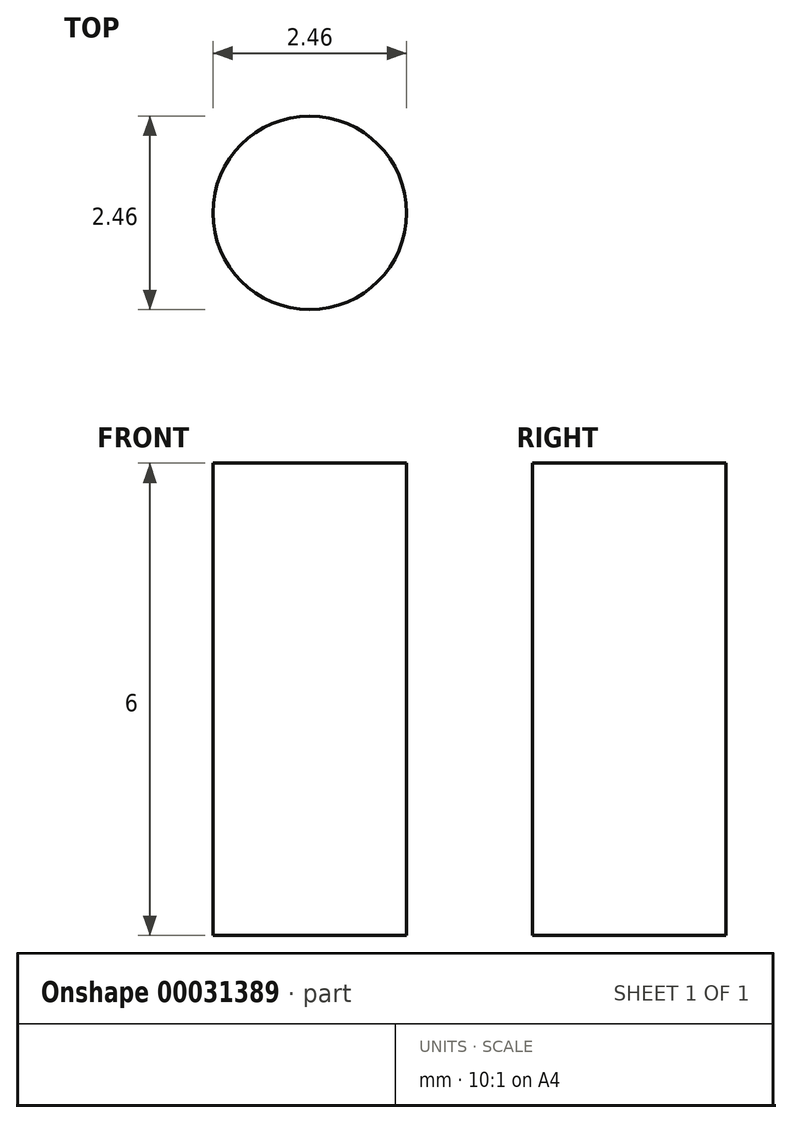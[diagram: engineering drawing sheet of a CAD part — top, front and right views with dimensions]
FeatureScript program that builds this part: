
annotation { "Feature Type Name" : "Feature", "Feature Type Description" : "" }
export const myFeature = defineFeature(function(context is Context, id is Id, definition is map)
    precondition{}
    {
        {
            var Q0;
            Q0=qCreatedBy(makeId("Top.planeOp"),FACE);
            var sketch = newSketch(context, id + "F0", { "sketchPlane" : qUnion([Q0])});
            skCircle(sketch, "E0", {"center": v(-104.5, -104.5) * mm, "radius": 1.23 * mm});
            skCircle(sketch, "E1", {"center": v(104.5, -104.5) * mm, "radius": 1.23 * mm});
            skCircle(sketch, "E2", {"center": v(104.5, 104.5) * mm, "radius": 1.23 * mm});
            skCircle(sketch, "E3", {"center": v(21, 0) * mm, "radius": 1.23 * mm});
            skCircle(sketch, "E4", {"center": v(-20, 0) * mm, "radius": 1.23 * mm});
            skCircle(sketch, "E5", {"center": v(-104.5, 104.5) * mm, "radius": 1.23 * mm});
            skLineSegment(sketch, "E6", {"start": v(75, -68) * mm, "end": v(35, -28) * mm});
            skLineSegment(sketch, "E7", {"start": v(75, 68) * mm, "end": v(75, -68) * mm});
            skLineSegment(sketch, "E8", {"start": v(35, 28) * mm, "end": v(75, 68) * mm});
            skLineSegment(sketch, "E9", {"start": v(35, -28) * mm, "end": v(35, 28) * mm});
            skLineSegment(sketch, "E10", {"start": v(-75, 68) * mm, "end": v(-35, 28) * mm});
            skLineSegment(sketch, "E11", {"start": v(-75, -68) * mm, "end": v(-75, 68) * mm});
            skLineSegment(sketch, "E12", {"start": v(-35, -28) * mm, "end": v(-75, -68) * mm});
            skLineSegment(sketch, "E13", {"start": v(-35, 28) * mm, "end": v(-35, -28) * mm});
            skLineSegment(sketch, "E14", {"start": v(5, -80) * mm, "end": v(-5, -80) * mm});
            skLineSegment(sketch, "E15", {"start": v(25, -60) * mm, "end": v(5, -80) * mm});
            skLineSegment(sketch, "E16", {"start": v(25, -40) * mm, "end": v(25, -60) * mm});
            skLineSegment(sketch, "E17", {"start": v(5, -20) * mm, "end": v(25, -40) * mm});
            skLineSegment(sketch, "E18", {"start": v(-5, -20) * mm, "end": v(5, -20) * mm});
            skLineSegment(sketch, "E19", {"start": v(-25, -40) * mm, "end": v(-5, -20) * mm});
            skLineSegment(sketch, "E20", {"start": v(-25, -60) * mm, "end": v(-25, -40) * mm});
            skLineSegment(sketch, "E21", {"start": v(-5, -80) * mm, "end": v(-25, -60) * mm});
            skLineSegment(sketch, "E22", {"start": v(-25, 40) * mm, "end": v(-25, 50) * mm});
            skLineSegment(sketch, "E23", {"start": v(-5, 20) * mm, "end": v(-25, 40) * mm});
            skLineSegment(sketch, "E24", {"start": v(5, 20) * mm, "end": v(-5, 20) * mm});
            skLineSegment(sketch, "E25", {"start": v(25, 40) * mm, "end": v(5, 20) * mm});
            skLineSegment(sketch, "E26", {"start": v(25, 50) * mm, "end": v(25, 40) * mm});
            skLineSegment(sketch, "E27", {"start": v(5, 70) * mm, "end": v(25, 50) * mm});
            skLineSegment(sketch, "E28", {"start": v(-5, 70) * mm, "end": v(5, 70) * mm});
            skLineSegment(sketch, "E29", {"start": v(-25, 50) * mm, "end": v(-5, 70) * mm});
            skArc(sketch, "E30", {"start": v(46, -90) * mm, "mid": v(48.83, -88.83) * mm, "end": v(50, -86) * mm});
            skLineSegment(sketch, "E31", {"start": v(50, -84) * mm, "end": v(50, -86) * mm});
            skArc(sketch, "E32", {"start": v(50, -84) * mm, "mid": v(48.83, -81.17) * mm, "end": v(46, -80) * mm});
            skLineSegment(sketch, "E33", {"start": v(23, -80) * mm, "end": v(46, -80) * mm});
            skArc(sketch, "E34", {"start": v(23, -80) * mm, "mid": v(20.17, -81.17) * mm, "end": v(19, -84) * mm});
            skLineSegment(sketch, "E35", {"start": v(19, -86) * mm, "end": v(19, -84) * mm});
            skArc(sketch, "E36", {"start": v(19, -86) * mm, "mid": v(20.17, -88.83) * mm, "end": v(23, -90) * mm});
            skLineSegment(sketch, "E37", {"start": v(46, -90) * mm, "end": v(23, -90) * mm});
            skArc(sketch, "E38", {"start": v(12.14, 80) * mm, "mid": v(14.97, 81.17) * mm, "end": v(16.14, 84) * mm});
            skLineSegment(sketch, "E39", {"start": v(16.14, 86) * mm, "end": v(16.14, 84) * mm});
            skArc(sketch, "E40", {"start": v(16.14, 86) * mm, "mid": v(14.97, 88.83) * mm, "end": v(12.14, 90) * mm});
            skLineSegment(sketch, "E41", {"start": v(-10.86, 90) * mm, "end": v(12.14, 90) * mm});
            skArc(sketch, "E42", {"start": v(-10.86, 90) * mm, "mid": v(-13.7, 88.83) * mm, "end": v(-14.86, 86) * mm});
            skLineSegment(sketch, "E43", {"start": v(-14.86, 84) * mm, "end": v(-14.86, 86) * mm});
            skArc(sketch, "E44", {"start": v(-14.86, 84) * mm, "mid": v(-13.7, 81.17) * mm, "end": v(-10.86, 80) * mm});
            skLineSegment(sketch, "E45", {"start": v(12.14, 80) * mm, "end": v(-10.86, 80) * mm});
            skArc(sketch, "E46", {"start": v(-24, -90) * mm, "mid": v(-21.18, -88.83) * mm, "end": v(-20, -86) * mm});
            skLineSegment(sketch, "E47", {"start": v(-20, -84) * mm, "end": v(-20, -86) * mm});
            skArc(sketch, "E48", {"start": v(-20, -84) * mm, "mid": v(-21.18, -81.17) * mm, "end": v(-24, -80) * mm});
            skLineSegment(sketch, "E49", {"start": v(-47, -80) * mm, "end": v(-24, -80) * mm});
            skArc(sketch, "E50", {"start": v(-47, -80) * mm, "mid": v(-49.84, -81.17) * mm, "end": v(-51, -84) * mm});
            skLineSegment(sketch, "E51", {"start": v(-51, -86) * mm, "end": v(-51, -84) * mm});
            skArc(sketch, "E52", {"start": v(-51, -86) * mm, "mid": v(-49.84, -88.83) * mm, "end": v(-47, -90) * mm});
            skLineSegment(sketch, "E53", {"start": v(-24, -90) * mm, "end": v(-47, -90) * mm});
            skLineSegment(sketch, "E54", {"start": v(-110, -107) * mm, "end": v(-107, -110) * mm});
            skLineSegment(sketch, "E55", {"start": v(-107, -110) * mm, "end": v(-103, -110) * mm});
            skLineSegment(sketch, "E56", {"start": v(-103, -110) * mm, "end": v(-83, -90) * mm});
            skLineSegment(sketch, "E57", {"start": v(-83, -90) * mm, "end": v(-63, -90) * mm});
            skLineSegment(sketch, "E58", {"start": v(-63, -90) * mm, "end": v(-53, -100) * mm});
            skLineSegment(sketch, "E59", {"start": v(-53, -100) * mm, "end": v(-15, -100) * mm});
            skLineSegment(sketch, "E60", {"start": v(-15, -100) * mm, "end": v(-5, -90) * mm});
            skLineSegment(sketch, "E61", {"start": v(-5, -90) * mm, "end": v(5, -90) * mm});
            skLineSegment(sketch, "E62", {"start": v(5, -90) * mm, "end": v(15, -100) * mm});
            skLineSegment(sketch, "E63", {"start": v(15, -100) * mm, "end": v(53, -100) * mm});
            skLineSegment(sketch, "E64", {"start": v(53, -100) * mm, "end": v(63, -90) * mm});
            skLineSegment(sketch, "E65", {"start": v(63, -90) * mm, "end": v(83, -90) * mm});
            skLineSegment(sketch, "E66", {"start": v(83, -90) * mm, "end": v(103, -110) * mm});
            skLineSegment(sketch, "E67", {"start": v(103, -110) * mm, "end": v(107, -110) * mm});
            skLineSegment(sketch, "E68", {"start": v(107, -110) * mm, "end": v(110, -107) * mm});
            skLineSegment(sketch, "E69", {"start": v(110, -107) * mm, "end": v(110, -103) * mm});
            skLineSegment(sketch, "E70", {"start": v(110, -103) * mm, "end": v(85, -78) * mm});
            skLineSegment(sketch, "E71", {"start": v(85, -78) * mm, "end": v(85, 78) * mm});
            skLineSegment(sketch, "E72", {"start": v(85, 78) * mm, "end": v(110, 103) * mm});
            skLineSegment(sketch, "E73", {"start": v(110, 103) * mm, "end": v(110, 107) * mm});
            skLineSegment(sketch, "E74", {"start": v(110, 107) * mm, "end": v(107, 110) * mm});
            skLineSegment(sketch, "E75", {"start": v(107, 110) * mm, "end": v(103, 110) * mm});
            skLineSegment(sketch, "E76", {"start": v(103, 110) * mm, "end": v(63, 70) * mm});
            skLineSegment(sketch, "E77", {"start": v(63, 70) * mm, "end": v(43, 70) * mm});
            skLineSegment(sketch, "E78", {"start": v(43, 70) * mm, "end": v(13, 100) * mm});
            skLineSegment(sketch, "E79", {"start": v(13, 100) * mm, "end": v(-13, 100) * mm});
            skLineSegment(sketch, "E80", {"start": v(-13, 100) * mm, "end": v(-43, 70) * mm});
            skLineSegment(sketch, "E81", {"start": v(-43, 70) * mm, "end": v(-63, 70) * mm});
            skLineSegment(sketch, "E82", {"start": v(-63, 70) * mm, "end": v(-103, 110) * mm});
            skLineSegment(sketch, "E83", {"start": v(-103, 110) * mm, "end": v(-107, 110) * mm});
            skLineSegment(sketch, "E84", {"start": v(-107, 110) * mm, "end": v(-110, 107) * mm});
            skLineSegment(sketch, "E85", {"start": v(-110, 107) * mm, "end": v(-110, 103) * mm});
            skLineSegment(sketch, "E86", {"start": v(-110, 103) * mm, "end": v(-85, 78) * mm});
            skLineSegment(sketch, "E87", {"start": v(-85, 78) * mm, "end": v(-85, -78) * mm});
            skLineSegment(sketch, "E88", {"start": v(-85, -78) * mm, "end": v(-110, -103) * mm});
            skLineSegment(sketch, "E89", {"start": v(-110, -103) * mm, "end": v(-110, -107) * mm});
            skLineSegment(sketch, "E90", {"start": v(-16.5, 8.2) * mm, "end": v(-16.5, -8.2) * mm});
            skLineSegment(sketch, "E91", {"start": v(-16.5, -8.2) * mm, "end": v(-11.5, -8.2) * mm});
            skLineSegment(sketch, "E92", {"start": v(-11.5, -8.2) * mm, "end": v(-11.5, -2.5) * mm});
            skLineSegment(sketch, "E93", {"start": v(-10.5, -1.5) * mm, "end": v(-2.66, -1.5) * mm});
            skLineSegment(sketch, "E94", {"start": v(-2.66, 1.5) * mm, "end": v(-10.5, 1.5) * mm});
            skLineSegment(sketch, "E95", {"start": v(-11.5, 2.5) * mm, "end": v(-11.5, 8.2) * mm});
            skLineSegment(sketch, "E96", {"start": v(-11.5, 8.2) * mm, "end": v(-16.5, 8.2) * mm});
            skLineSegment(sketch, "E97", {"start": v(3.66, 1.5) * mm, "end": v(11.5, 1.5) * mm});
            skLineSegment(sketch, "E98", {"start": v(12.5, 2.5) * mm, "end": v(12.5, 8.2) * mm});
            skLineSegment(sketch, "E99", {"start": v(12.5, 8.2) * mm, "end": v(17.5, 8.2) * mm});
            skLineSegment(sketch, "E100", {"start": v(17.5, 8.2) * mm, "end": v(17.5, -8.2) * mm});
            skLineSegment(sketch, "E101", {"start": v(17.5, -8.2) * mm, "end": v(12.5, -8.2) * mm});
            skLineSegment(sketch, "E102", {"start": v(12.5, -8.2) * mm, "end": v(12.5, -2.5) * mm});
            skLineSegment(sketch, "E103", {"start": v(11.5, -1.5) * mm, "end": v(3.66, -1.5) * mm});
            skArc(sketch, "E104", {"start": v(-11.5, 2.5) * mm, "mid": v(-11.2, 1.8) * mm, "end": v(-10.5, 1.5) * mm});
            skArc(sketch, "E105", {"start": v(-10.5, -1.5) * mm, "mid": v(-11.2, -1.8) * mm, "end": v(-11.5, -2.5) * mm});
            skArc(sketch, "E106", {"start": v(-2.66, -1.5) * mm, "mid": v(0.5, -3.5) * mm, "end": v(3.66, -1.5) * mm});
            skArc(sketch, "E107", {"start": v(3.66, 1.5) * mm, "mid": v(0.5, 3.5) * mm, "end": v(-2.66, 1.5) * mm});
            skArc(sketch, "E108", {"start": v(11.5, 1.5) * mm, "mid": v(12.2, 1.8) * mm, "end": v(12.5, 2.5) * mm});
            skArc(sketch, "E109", {"start": v(12.5, -2.5) * mm, "mid": v(12.2, -1.8) * mm, "end": v(11.5, -1.5) * mm});
            skCircle(sketch, "E110", {"center": v(-35, -75) * mm, "radius": 1.5 * mm});
            skCircle(sketch, "E111", {"center": v(-35, -95) * mm, "radius": 1.5 * mm});
            skCircle(sketch, "E112", {"center": v(35, -95) * mm, "radius": 1.5 * mm});
            skCircle(sketch, "E113", {"center": v(35, -75) * mm, "radius": 1.5 * mm});
            skCircle(sketch, "E114", {"center": v(0, 75) * mm, "radius": 1.5 * mm});
            skCircle(sketch, "E115", {"center": v(0, 95) * mm, "radius": 1.5 * mm});
            skSolve(sketch);
        }
        {
            var Q0;
            Q0=makeQuery(id+"F0.imprint","IMPRINT",FACE,{"disambiguationData":[TD([[makeQuery(id+"F0.imprint","IMPRINT",EDGE,{"derivedFrom":sQuery(id+"F0.wireOp",EDGE,"E0")}),1.0]])]});
            extrude(context, id + "F1", {"entities" : qUnion([Q0]), "depth" : 6 * mm});
        }
    });
